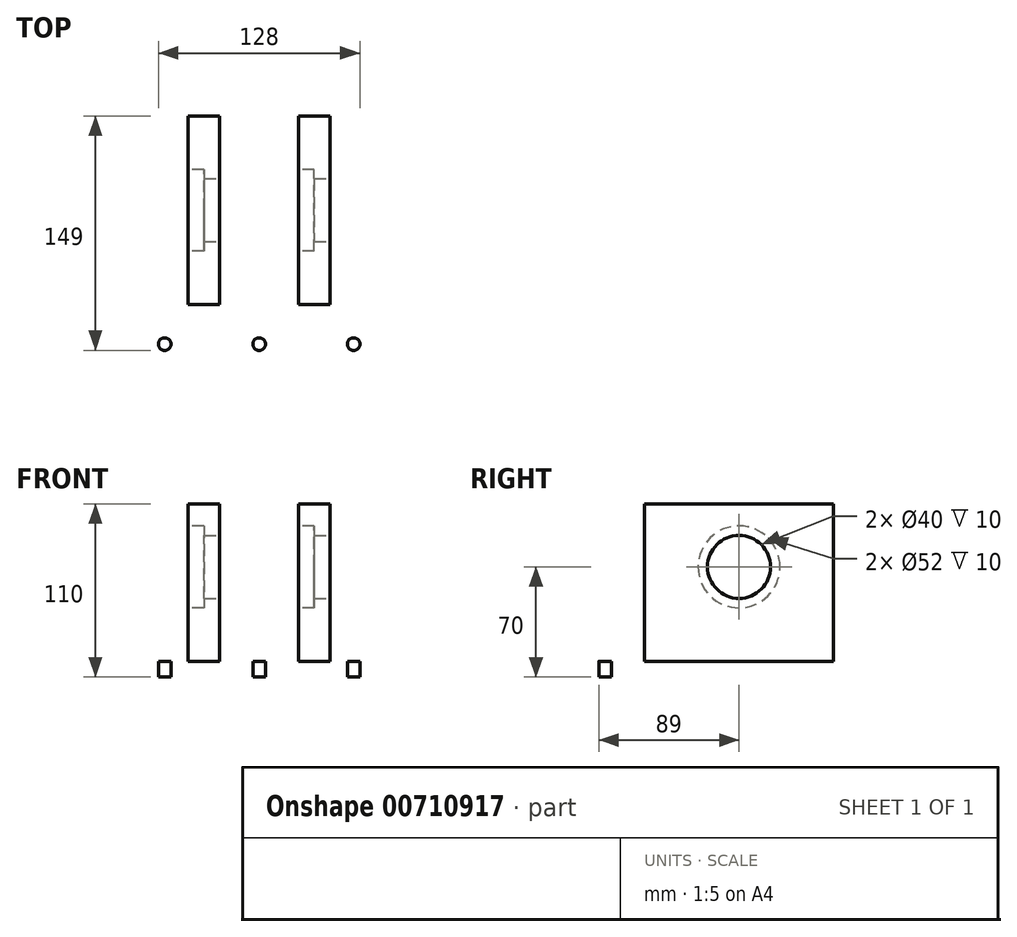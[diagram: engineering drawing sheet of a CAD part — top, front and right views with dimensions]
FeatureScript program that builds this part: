
annotation { "Feature Type Name" : "Feature", "Feature Type Description" : "" }
export const myFeature = defineFeature(function(context is Context, id is Id, definition is map)
    precondition{}
    {
        {
            var Q0;
            Q0=qCreatedBy(makeId("Top.planeOp"),FACE);
            var sketch = newSketch(context, id + "F0", { "sketchPlane" : qUnion([Q0])});
            skLineSegment(sketch, "E0.bottom", {"start": v(72.5, 100) * mm, "end": v(-72.5, 100) * mm});
            skLineSegment(sketch, "E0.top", {"start": v(72.5, -100) * mm, "end": v(-72.5, -100) * mm});
            skLineSegment(sketch, "E0.left", {"start": v(72.5, 100) * mm, "end": v(72.5, -100) * mm});
            skLineSegment(sketch, "E0.right", {"start": v(-72.5, 100) * mm, "end": v(-72.5, -100) * mm});
            skPoint(sketch, "E0.middle", {"position": v(0, 0) * mm});
            skSolve(sketch);
        }
        {
            var Q0;
            Q0=makeQuery(id+"F0.imprint","IMPRINT",FACE,{"disambiguationData":[TD([[makeQuery(id+"F0.imprint","IMPRINT",EDGE,{"derivedFrom":sQuery(id+"F0.wireOp",EDGE,"E0.bottom")}),1.0]])]});
            extrude(context, id + "F1", {"entities" : qUnion([Q0]), "oppositeDirection" : true, "depth" : 10 * mm, "offsetDistance" : 25 * mm});
        }
        {
            var Q0;
            Q0=makeQuery(id+"F1.opExtrude","CAP_FACE",FACE,{"disambiguationData":[OSD([sQuery(id+"F0.wireOp",EDGE,"E0.bottom"),sQuery(id+"F0.wireOp",EDGE,"E0.top"),sQuery(id+"F0.wireOp",EDGE,"E0.left"),sQuery(id+"F0.wireOp",EDGE,"E0.right")])],"isStart":true});
            var sketch = newSketch(context, id + "F2", { "sketchPlane" : qUnion([Q0])});
            skLineSegment(sketch, "E1", {"start": v(0, 100) * mm, "end": v(0, -100) * mm, "construction": true});
            skLineSegment(sketch, "E2", {"start": v(-72.5, 85) * mm, "end": v(72.5, 85) * mm, "construction": true});
            skCircle(sketch, "E3", {"center": v(0, 85) * mm, "radius": 4 * mm});
            skCircle(sketch, "E4", {"center": v(-60, 85) * mm, "radius": 4 * mm});
            skCircle(sketch, "E5", {"center": v(60, 85) * mm, "radius": 4 * mm});
            skCircle(sketch, "E6.MirrorC", {"center": v(-60, -85) * mm, "radius": 4 * mm});
            skCircle(sketch, "E7.MirrorC", {"center": v(0, -85) * mm, "radius": 4 * mm});
            skCircle(sketch, "E8.MirrorC", {"center": v(60, -85) * mm, "radius": 4 * mm});
            skSolve(sketch);
        }
        {
            var Q0;
            Q0=makeQuery(id+"F2.imprint","IMPRINT",FACE,{"disambiguationData":[TD([[makeQuery(id+"F2.imprint","IMPRINT",EDGE,{"derivedFrom":sQuery(id+"F2.wireOp",EDGE,"E4")}),1.0]])]});
            var Q1;
            Q1=makeQuery(id+"F2.imprint","IMPRINT",FACE,{"disambiguationData":[TD([[makeQuery(id+"F2.imprint","IMPRINT",EDGE,{"derivedFrom":sQuery(id+"F2.wireOp",EDGE,"E3")}),1.0]])]});
            var Q2;
            Q2=makeQuery(id+"F2.imprint","IMPRINT",FACE,{"disambiguationData":[TD([[makeQuery(id+"F2.imprint","IMPRINT",EDGE,{"derivedFrom":sQuery(id+"F2.wireOp",EDGE,"E5")}),1.0]])]});
            var Q3;
            Q3=makeQuery(id+"F2.imprint","IMPRINT",FACE,{"disambiguationData":[TD([[makeQuery(id+"F2.imprint","IMPRINT",EDGE,{"derivedFrom":sQuery(id+"F2.wireOp",EDGE,"E8.MirrorC")}),-1.0]])]});
            var Q4;
            Q4=makeQuery(id+"F2.imprint","IMPRINT",FACE,{"disambiguationData":[TD([[makeQuery(id+"F2.imprint","IMPRINT",EDGE,{"derivedFrom":sQuery(id+"F2.wireOp",EDGE,"E7.MirrorC")}),-1.0]])]});
            var Q5;
            Q5=makeQuery(id+"F2.imprint","IMPRINT",FACE,{"disambiguationData":[TD([[makeQuery(id+"F2.imprint","IMPRINT",EDGE,{"derivedFrom":sQuery(id+"F2.wireOp",EDGE,"E6.MirrorC")}),-1.0]])]});
            extrude(context, id + "F3", {"entities" : qUnion([Q0, Q1, Q2, Q3, Q4, Q5]), "operationType" : NewBodyOperationType.REMOVE, "oppositeDirection" : true, "depth" : 10 * mm, "offsetDistance" : 25 * mm});
        }
        {
            var Q0;
            Q0=makeQuery(id+"F1.opExtrude","CAP_FACE",FACE,{"disambiguationData":[OSD([sQuery(id+"F0.wireOp",EDGE,"E0.bottom"),sQuery(id+"F0.wireOp",EDGE,"E0.top"),sQuery(id+"F0.wireOp",EDGE,"E0.left"),sQuery(id+"F0.wireOp",EDGE,"E0.right")])],"isStart":true});
            var sketch = newSketch(context, id + "F4", { "sketchPlane" : qUnion([Q0])});
            skLineSegment(sketch, "E9.bottom", {"start": v(-25, 60) * mm, "end": v(-45, 60) * mm});
            skLineSegment(sketch, "E9.top", {"start": v(-25, -60) * mm, "end": v(-45, -60) * mm});
            skLineSegment(sketch, "E9.left", {"start": v(-25, 60) * mm, "end": v(-25, -60) * mm});
            skLineSegment(sketch, "E9.right", {"start": v(-45, 60) * mm, "end": v(-45, -60) * mm});
            skPoint(sketch, "E9.middle", {"position": v(-35, 0) * mm});
            skLineSegment(sketch, "E10.bottom", {"start": v(45, 60) * mm, "end": v(25, 60) * mm});
            skLineSegment(sketch, "E10.top", {"start": v(45, -60) * mm, "end": v(25, -60) * mm});
            skLineSegment(sketch, "E10.left", {"start": v(45, 60) * mm, "end": v(45, -60) * mm});
            skLineSegment(sketch, "E10.right", {"start": v(25, 60) * mm, "end": v(25, -60) * mm});
            skPoint(sketch, "E10.middle", {"position": v(35, 0) * mm});
            skSolve(sketch);
        }
        {
            var Q0;
            Q0=makeQuery(id+"F4.imprint","IMPRINT",FACE,{"disambiguationData":[TD([[makeQuery(id+"F4.imprint","IMPRINT",EDGE,{"derivedFrom":sQuery(id+"F4.wireOp",EDGE,"E9.bottom")}),1.0]])]});
            var Q1;
            Q1=makeQuery(id+"F4.imprint","IMPRINT",FACE,{"disambiguationData":[TD([[makeQuery(id+"F4.imprint","IMPRINT",EDGE,{"derivedFrom":sQuery(id+"F4.wireOp",EDGE,"E10.bottom")}),1.0]])]});
            extrude(context, id + "F5", {"entities" : qUnion([Q0, Q1]), "operationType" : NewBodyOperationType.ADD, "depth" : 100 * mm, "offsetDistance" : 25 * mm});
        }
        {
            var Q0;
            Q0=makeQuery(id+"F5.opExtrude","SWEPT_FACE",FACE,{"disambiguationData":[OSD([sQuery(id+"F4.wireOp",EDGE,"E10.left")])]});
            var sketch = newSketch(context, id + "F6", { "sketchPlane" : qUnion([Q0])});
            skCircle(sketch, "E11", {"center": v(0, 60) * mm, "radius": 20 * mm});
            skSolve(sketch);
        }
        {
            var Q0;
            Q0=makeQuery(id+"F6.imprint","IMPRINT",FACE,{"disambiguationData":[TD([[makeQuery(id+"F6.imprint","IMPRINT",EDGE,{"derivedFrom":sQuery(id+"F6.wireOp",EDGE,"E11")}),1.0]])]});
            extrude(context, id + "F7", {"entities" : qUnion([Q0]), "operationType" : NewBodyOperationType.REMOVE, "oppositeDirection" : true, "depth" : 10 * mm, "offsetDistance" : 25 * mm});
        }
        {
            var Q0;
            Q0=makeQuery(id+"F5.opExtrude","SWEPT_FACE",FACE,{"disambiguationData":[OSD([sQuery(id+"F4.wireOp",EDGE,"E10.right")])]});
            var sketch = newSketch(context, id + "F8", { "sketchPlane" : qUnion([Q0])});
            skCircle(sketch, "E12", {"center": v(0, 60) * mm, "radius": 26 * mm});
            skSolve(sketch);
        }
        {
            var Q0;
            Q0=makeQuery(id+"F8.imprint","IMPRINT",FACE,{"disambiguationData":[TD([[makeQuery(id+"F8.imprint","IMPRINT",EDGE,{"derivedFrom":sQuery(id+"F8.wireOp",EDGE,"E12")}),1.0]])]});
            extrude(context, id + "F9", {"entities" : qUnion([Q0]), "operationType" : NewBodyOperationType.REMOVE, "oppositeDirection" : true, "depth" : 10 * mm, "offsetDistance" : 25 * mm});
        }
        {
            var Q0;
            Q0=makeQuery(id+"F5.opExtrude","SWEPT_FACE",FACE,{"disambiguationData":[OSD([sQuery(id+"F4.wireOp",EDGE,"E9.left")])]});
            var sketch = newSketch(context, id + "F10", { "sketchPlane" : qUnion([Q0])});
            skCircle(sketch, "E13", {"center": v(0, 60) * mm, "radius": 20 * mm});
            skSolve(sketch);
        }
        {
            var Q0;
            Q0=makeQuery(id+"F10.imprint","IMPRINT",FACE,{"disambiguationData":[TD([[makeQuery(id+"F10.imprint","IMPRINT",EDGE,{"derivedFrom":sQuery(id+"F10.wireOp",EDGE,"E13")}),1.0]])]});
            extrude(context, id + "F11", {"entities" : qUnion([Q0]), "operationType" : NewBodyOperationType.REMOVE, "oppositeDirection" : true, "depth" : 10 * mm, "offsetDistance" : 25 * mm});
        }
        {
            var Q0;
            Q0=makeQuery(id+"F5.opExtrude","SWEPT_FACE",FACE,{"disambiguationData":[OSD([sQuery(id+"F4.wireOp",EDGE,"E9.right")])]});
            var sketch = newSketch(context, id + "F12", { "sketchPlane" : qUnion([Q0])});
            skCircle(sketch, "E14", {"center": v(0, 60) * mm, "radius": 26 * mm});
            skSolve(sketch);
        }
        {
            var Q0;
            Q0=makeQuery(id+"F12.imprint","IMPRINT",FACE,{"disambiguationData":[TD([[makeQuery(id+"F12.imprint","IMPRINT",EDGE,{"derivedFrom":sQuery(id+"F12.wireOp",EDGE,"E14")}),1.0]])]});
            extrude(context, id + "F13", {"entities" : qUnion([Q0]), "operationType" : NewBodyOperationType.REMOVE, "oppositeDirection" : true, "depth" : 10 * mm, "offsetDistance" : 25 * mm});
        }
    });
